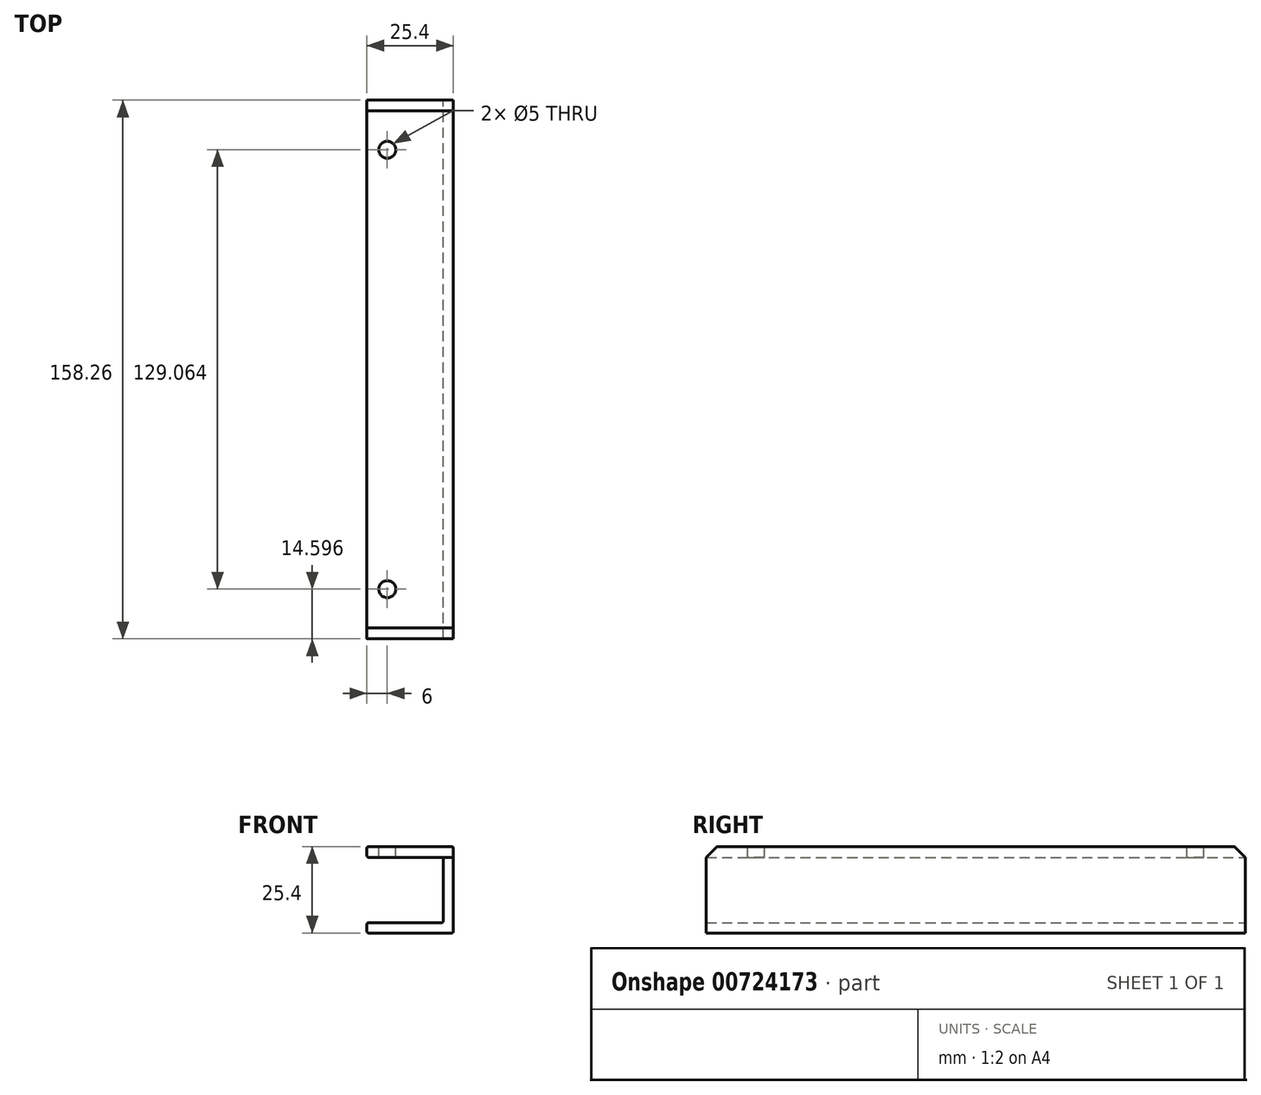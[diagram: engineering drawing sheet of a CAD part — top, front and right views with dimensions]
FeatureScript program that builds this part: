
annotation { "Feature Type Name" : "Feature", "Feature Type Description" : "" }
export const myFeature = defineFeature(function(context is Context, id is Id, definition is map)
    precondition{}
    {
        {
            var Q0;
            Q0=qCreatedBy(makeId("Front.planeOp"),FACE);
            var sketch = newSketch(context, id + "F0", { "sketchPlane" : qUnion([Q0])});
            skLineSegment(sketch, "E0", {"start": v(0, 0) * mm, "end": v(25.4, 0) * mm});
            skLineSegment(sketch, "E1", {"start": v(25.4, 0) * mm, "end": v(25.4, 25.4) * mm});
            skLineSegment(sketch, "E2", {"start": v(25.4, 25.4) * mm, "end": v(0, 25.4) * mm});
            skLineSegment(sketch, "E3", {"start": v(0, 25.4) * mm, "end": v(0, 22.22) * mm});
            skLineSegment(sketch, "E4", {"start": v(0, 22.22) * mm, "end": v(22.4, 22.23) * mm});
            skLineSegment(sketch, "E5", {"start": v(22.4, 22.23) * mm, "end": v(22.4, 3) * mm});
            skLineSegment(sketch, "E6", {"start": v(22.4, 3) * mm, "end": v(0, 3) * mm});
            skLineSegment(sketch, "E7", {"start": v(0, 3) * mm, "end": v(0, 0) * mm});
            skSolve(sketch);
        }
        {
            var Q0;
            Q0=makeQuery(id+"F0.imprint","IMPRINT",FACE,{"disambiguationData":[TD([[makeQuery(id+"F0.imprint","IMPRINT",EDGE,{"derivedFrom":sQuery(id+"F0.wireOp",EDGE,"E0")}),1.0]])]});
            extrude(context, id + "F1", {"entities" : qUnion([Q0]), "depth" : (159.06 - 0.8) * mm, "offsetDistance" : 25 * mm});
        }
        {
            var Q0;
            Q0=makeQuery(id+"F1.opExtrude","SWEPT_FACE",FACE,{"disambiguationData":[OSD([sQuery(id+"F0.wireOp",EDGE,"E2")])]});
            var sketch = newSketch(context, id + "F2", { "sketchPlane" : qUnion([Q0])});
            skLineSegment(sketch, "E8", {"start": v(6, 0) * mm, "end": v(6, -158.26) * mm, "construction": true});
            skCircle(sketch, "E9", {"center": v(6, -14.6) * mm, "radius": 2.5 * mm});
            skCircle(sketch, "E10", {"center": v(6, -143.66) * mm, "radius": 2.5 * mm});
            skCircle(sketch, "E11", {"center": v(6, -243.66) * mm, "radius": 2.5 * mm});
            skCircle(sketch, "E12", {"center": v(6, -343.66) * mm, "radius": 2.5 * mm});
            skCircle(sketch, "E13", {"center": v(6, -443.66) * mm, "radius": 2.5 * mm});
            skSolve(sketch);
        }
        {
            var Q0;
            Q0 = qSketchRegion(id + "F2", true);
            extrude(context, id + "F3", {"entities" : qUnion([Q0]), "operationType" : NewBodyOperationType.REMOVE, "oppositeDirection" : true, "depth" : 5 * mm, "offsetDistance" : 25 * mm});
        }
        {
            var Q0;
            Q0=makeQuery(id+"F1.opExtrude","SWEPT_EDGE",EDGE,{"disambiguationData":[OSD([sQuery(id+"F0.wireOp",EDGE,"E2"),sQuery(id+"F0.wireOp",EDGE,"E3")])]});
            var Q1;
            Q1=makeQuery(id+"F1.opExtrude","SWEPT_EDGE",EDGE,{"disambiguationData":[OSD([sQuery(id+"F0.wireOp",EDGE,"E3"),sQuery(id+"F0.wireOp",EDGE,"E4")])]});
            var Q2;
            Q2=makeQuery(id+"F1.opExtrude","SWEPT_EDGE",EDGE,{"disambiguationData":[OSD([sQuery(id+"F0.wireOp",EDGE,"E1"),sQuery(id+"F0.wireOp",EDGE,"E2")])]});
            var Q3;
            Q3=makeQuery(id+"F1.opExtrude","SWEPT_EDGE",EDGE,{"disambiguationData":[OSD([sQuery(id+"F0.wireOp",EDGE,"E5"),sQuery(id+"F0.wireOp",EDGE,"E6")])]});
            var Q4;
            Q4=makeQuery(id+"F1.opExtrude","SWEPT_EDGE",EDGE,{"disambiguationData":[OSD([sQuery(id+"F0.wireOp",EDGE,"E6"),sQuery(id+"F0.wireOp",EDGE,"E7")])]});
            var Q5;
            Q5=makeQuery(id+"F1.opExtrude","SWEPT_EDGE",EDGE,{"disambiguationData":[OSD([sQuery(id+"F0.wireOp",EDGE,"E0"),sQuery(id+"F0.wireOp",EDGE,"E7")])]});
            var Q6;
            Q6=makeQuery(id+"F1.opExtrude","SWEPT_EDGE",EDGE,{"disambiguationData":[OSD([sQuery(id+"F0.wireOp",EDGE,"E4"),sQuery(id+"F0.wireOp",EDGE,"E5")])]});
            var Q7;
            Q7=makeQuery(id+"F1.opExtrude","SWEPT_EDGE",EDGE,{"disambiguationData":[OSD([sQuery(id+"F0.wireOp",EDGE,"E0"),sQuery(id+"F0.wireOp",EDGE,"E1")])]});
            fillet(context, id + "F4", {"entities" : qUnion([Q0, Q1, Q2, Q3, Q4, Q5, Q6, Q7]), "radius" : 0.5 * mm, "tangentPropagation" : true, "allowEdgeOverflow" : false});
        }
        {
            var Q0;
            Q0=makeQuery(id+"F1.opExtrude","SWEPT_FACE",FACE,{"disambiguationData":[OSD([sQuery(id+"F0.wireOp",EDGE,"E3")])]});
            var sketch = newSketch(context, id + "F5", { "sketchPlane" : qUnion([Q0])});
            skLineSegment(sketch, "E14", {"start": v(0, 22.22) * mm, "end": v(0, 25.4) * mm});
            skLineSegment(sketch, "E15", {"start": v(0, 25.4) * mm, "end": v(3.17, 25.4) * mm});
            skLineSegment(sketch, "E16", {"start": v(3.17, 25.4) * mm, "end": v(0, 22.22) * mm});
            skLineSegment(sketch, "E17", {"start": v(158.26, 22.22) * mm, "end": v(158.26, 25.4) * mm});
            skLineSegment(sketch, "E18", {"start": v(158.26, 25.4) * mm, "end": v(155.09, 25.4) * mm});
            skLineSegment(sketch, "E19", {"start": v(155.09, 25.4) * mm, "end": v(158.26, 22.22) * mm});
            skSolve(sketch);
        }
        {
            var Q0;
            Q0 = qSketchRegion(id + "F5", true);
            extrude(context, id + "F6", {"entities" : qUnion([Q0]), "operationType" : NewBodyOperationType.REMOVE, "endBound" : BoundingType.THROUGH_ALL, "oppositeDirection" : true, "depth" : 25 * mm, "offsetDistance" : 25 * mm});
        }
    });
